# Revit family: Ферма подстропильная 12 м_10%
name_source: partatom
category: Каркас несущий
units: mm (PartAtom-declared; Revit-internal decimal feet)

## family parameters
Всегда вертикально = Да
Всегда экспортировать в виде геометрии = Нет
Заголовок OmniClass = Trussed Beams and Joists
Материал для поведения модели = Сталь
На основе рабочей плоскости = Нет
Номер OmniClass = 23.25.30.21.14
Общий = Нет
Показывать семейство разрезанным на планах = Да
При загрузке вырезать с полостями = Нет
Условное обозначение = Из семейства
Форма сечения = Не задано

## types (9) — shared parameters
ADSK_Группа конструкций = 4
ADSK_Тип элемента КМ = 1

## per-type parameters (varying)
| type | ADSK_Марка конструкции | ADSK_Масса | Ферма ФП-12-10-36 | Ферма ФП-12-10-42 | Ферма ФП-12-10-44,4 | Ферма ФП-12-10-48,5 | Ферма ФП-12-10-53,0 | Ферма ФП-12-10-55 | Ферма ФП-12-10-59,9 | Ферма ФП-12-10-62,1 | Ферма ФП-12-10-71,2 |
| Ферма ФП-12-10-36 | ФП-12-10-36 | 960 | Да | Нет | Нет | Нет | Нет | Нет | Нет | Нет | Да |
| Ферма ФП-12-10-55 | ФП-12-10-55 | 1185 | Нет | Нет | Нет | Нет | Нет | Да | Нет | Нет | Да |
| Ферма ФП-12-10-42 | ФП-12-10-42 | 1052 | Нет | Да | Нет | Нет | Нет | Нет | Нет | Нет | Да |
| Ферма ФП-12-10-44,4 | ФП-12-10-44,4 | 914 | Нет | Нет | Да | Нет | Нет | Нет | Нет | Нет | Нет |
| Ферма ФП-12-10-48,5 | ФП-12-10-48,5 | 938 | Нет | Нет | Нет | Да | Нет | Нет | Нет | Нет | Нет |
| Ферма ФП-12-10-53,0 | ФП-12-10-53,0 | 958 | Нет | Нет | Нет | Нет | Да | Нет | Нет | Нет | Нет |
| Ферма ФП-12-10-59,9 | ФП-12-10-59,9 | 1104 | Нет | Нет | Нет | Нет | Нет | Нет | Да | Нет | Нет |
| Ферма ФП-12-10-62,1 | ФП-12-10-62,1 | 1157 | Нет | Нет | Нет | Нет | Нет | Нет | Нет | Да | Нет |
| Ферма ФП-12-10-71,2 | ФП-12-10-71,2 | 1271 | Нет | Нет | Нет | Нет | Нет | Нет | Нет | Нет | Да |

note: column(s) folded — value = type name in every type: ADSK_Наименование
